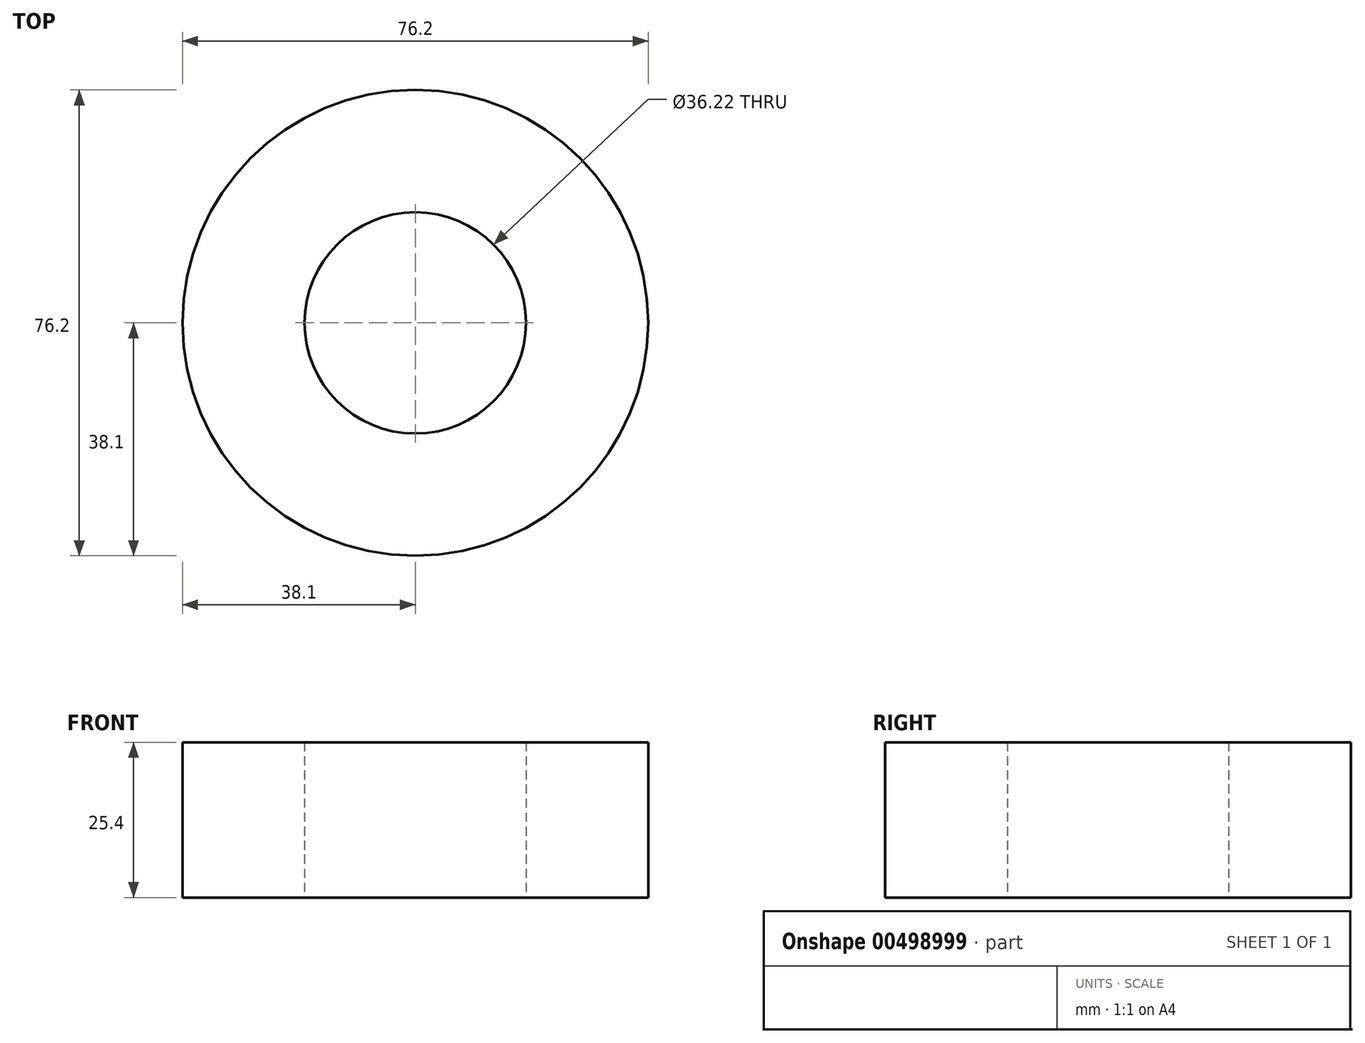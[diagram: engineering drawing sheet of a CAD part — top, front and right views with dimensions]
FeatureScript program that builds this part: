
annotation { "Feature Type Name" : "Feature", "Feature Type Description" : "" }
export const myFeature = defineFeature(function(context is Context, id is Id, definition is map)
    precondition{}
    {
        {
            var Q0;
            Q0=qCreatedBy(makeId("Top.planeOp"),FACE);
            var sketch = newSketch(context, id + "F0", { "sketchPlane" : qUnion([Q0])});
            skCircle(sketch, "E0", {"center": v(0, 0) * mm, "radius": 38.1 * mm});
            skCircle(sketch, "E1", {"center": v(0, 0) * mm, "radius": 18.1 * mm});
            skSolve(sketch);
        }
        {
            var Q0;
            Q0 = qSketchRegion(id + "F0", true);
            extrude(context, id + "F1", {"entities" : qUnion([Q0]), "depth" : 25.4 * mm});
        }
    });
